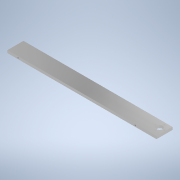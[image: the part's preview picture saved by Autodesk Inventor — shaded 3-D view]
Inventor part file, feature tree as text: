
AUTODESK INVENTOR PART (.ipt)
format: ipt  version: 2022 (Build 260153000, 153)  size: 141,312 bytes
history: native  units: mm
features: sketch x4, hole x3, other x1, extrude x1
ambient origin geometry x8: Origin, YZ Plane, XZ Plane, XY Plane, X Axis, Y Axis, Z Axis, Center Point
bodies: Body1 (feature_tree)
feature tree (9):
  other  "ソリッド1"
  extrude  "押し出し1"  Depth=30.0mm
  hole  "穴1"  [1 undecoded]
  hole  "穴3"  [1 undecoded]
  hole  "穴4"  [1 undecoded]
  sketch  "スケッチ1"
  sketch  "スケッチ2"
  sketch  "スケッチ4"
  sketch  "スケッチ5"
note: 3 required parameter values undecoded (feature->parameter linkage not recoverable at this tier; creation-order binding heuristic only, values carry confidence <= 0.55)
